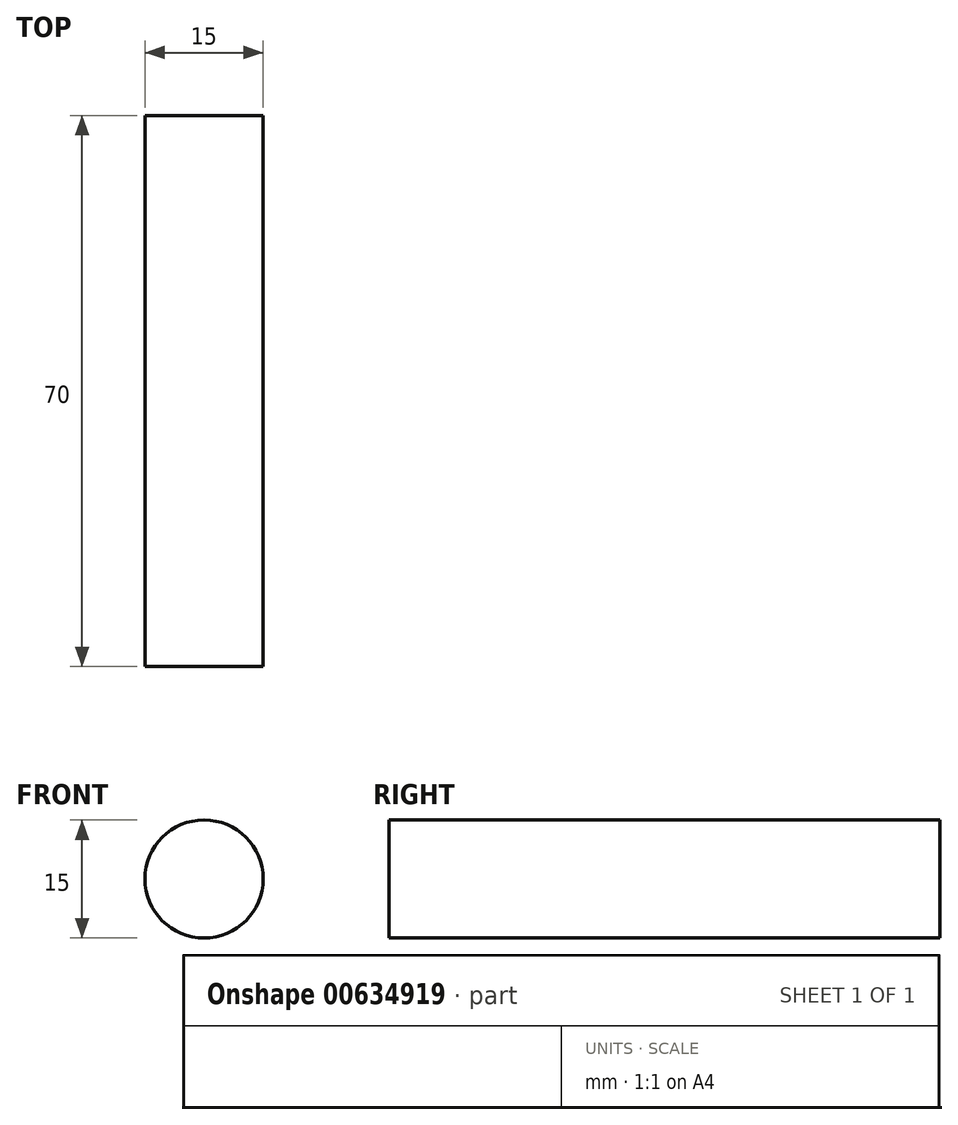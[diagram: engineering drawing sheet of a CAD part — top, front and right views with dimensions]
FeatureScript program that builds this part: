
annotation { "Feature Type Name" : "Feature", "Feature Type Description" : "" }
export const myFeature = defineFeature(function(context is Context, id is Id, definition is map)
    precondition{}
    {
        {
            var Q0;
            Q0=qCreatedBy(makeId("Front.planeOp"),FACE);
            var sketch = newSketch(context, id + "F0", { "sketchPlane" : qUnion([Q0])});
            skCircle(sketch, "E0", {"center": v(0, 0) * mm, "radius": 7.5 * mm});
            skSolve(sketch);
        }
        {
            var Q0;
            Q0 = qSketchRegion(id + "F0", true);
            extrude(context, id + "F1", {"entities" : qUnion([Q0]), "depth" : 70 * mm, "offsetDistance" : 25 * mm});
        }
    });
